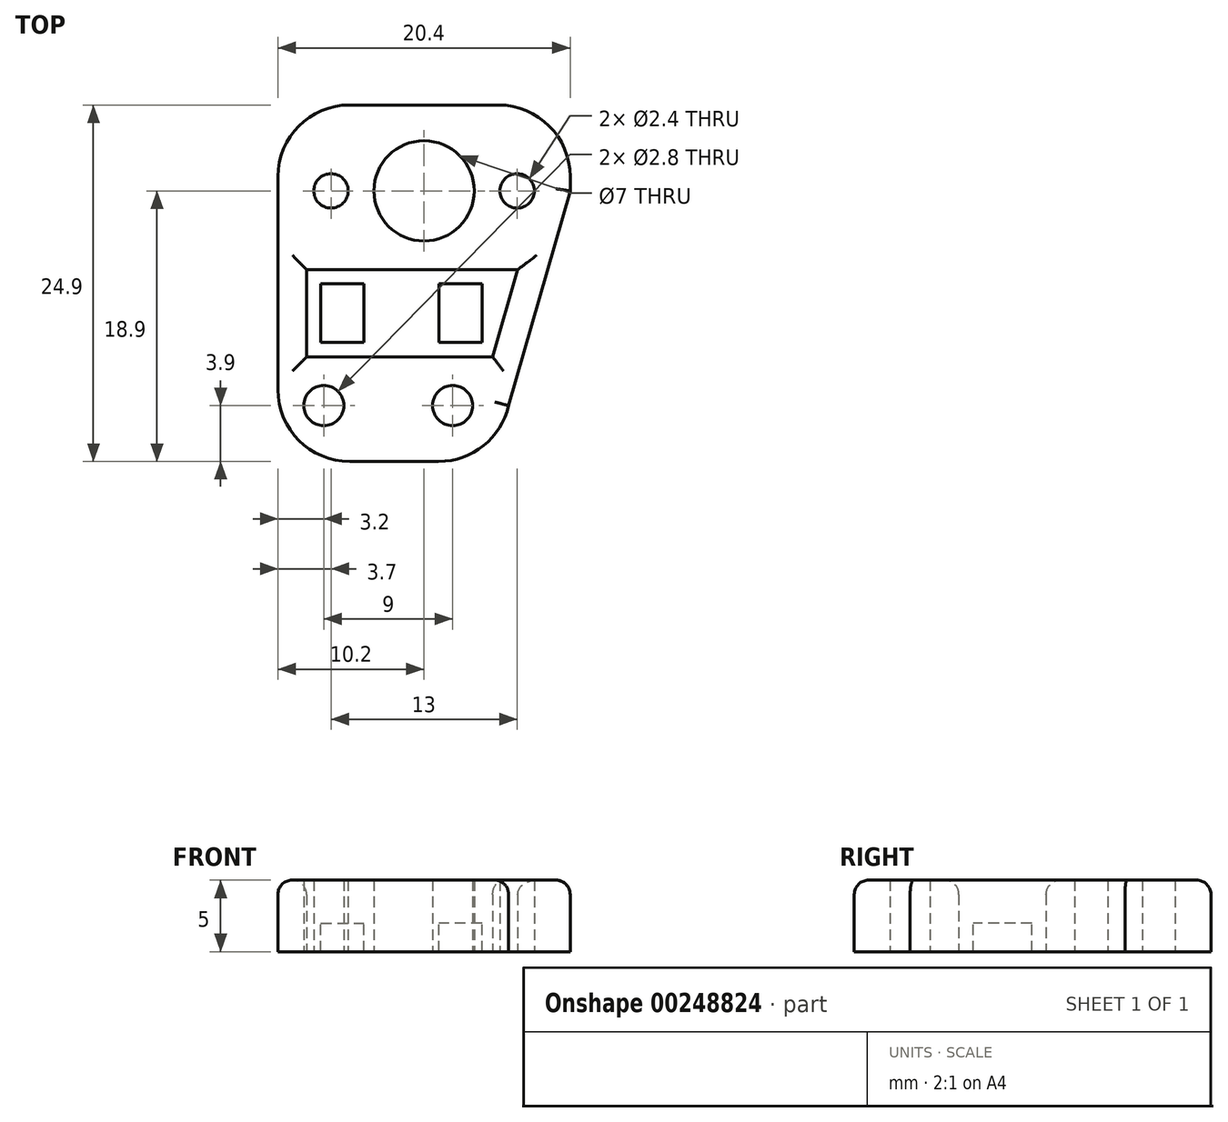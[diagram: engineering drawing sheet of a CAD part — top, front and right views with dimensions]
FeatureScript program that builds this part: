
annotation { "Feature Type Name" : "Feature", "Feature Type Description" : "" }
export const myFeature = defineFeature(function(context is Context, id is Id, definition is map)
    precondition{}
    {
        {
            var Q0;
            Q0=qCreatedBy(makeId("Top.planeOp"),FACE);
            var sketch = newSketch(context, id + "F0", { "sketchPlane" : qUnion([Q0])});
            skCircle(sketch, "E0", {"center": v(0, 0) * mm, "radius": 3.5 * mm});
            skCircle(sketch, "E1", {"center": v(-6.5, 0) * mm, "radius": 1.2 * mm});
            skCircle(sketch, "E2.MirrorC", {"center": v(6.5, 0) * mm, "radius": 1.2 * mm});
            skCircle(sketch, "E3", {"center": v(2, -15) * mm, "radius": 1.4 * mm});
            skCircle(sketch, "E4", {"center": v(-7, -15) * mm, "radius": 1.4 * mm});
            skLineSegment(sketch, "E5", {"start": v(-10.2, 6) * mm, "end": v(-10.2, -18.9) * mm});
            skLineSegment(sketch, "E6", {"start": v(-10.2, -18.9) * mm, "end": v(5.9, -18.9) * mm});
            skLineSegment(sketch, "E7", {"start": v(5.9, -18.9) * mm, "end": v(5.9, -15) * mm});
            skLineSegment(sketch, "E8", {"start": v(-10.2, 6) * mm, "end": v(10.2, 6) * mm});
            skLineSegment(sketch, "E9", {"start": v(10.2, 6) * mm, "end": v(10.2, 0) * mm});
            skLineSegment(sketch, "E10", {"start": v(10.2, 0) * mm, "end": v(5.9, -15) * mm});
            skLineSegment(sketch, "E11", {"start": v(-8.2, -11.6) * mm, "end": v(-8.2, -5.5) * mm});
            skLineSegment(sketch, "E12", {"start": v(-8.2, -5.5) * mm, "end": v(6.54, -5.5) * mm});
            skLineSegment(sketch, "E13", {"start": v(6.54, -5.5) * mm, "end": v(4.8, -11.6) * mm});
            skLineSegment(sketch, "E14", {"start": v(4.8, -11.6) * mm, "end": v(-8.2, -11.6) * mm});
            skSolve(sketch);
        }
        {
            var Q0;
            Q0=makeQuery(id+"F0.imprint","IMPRINT",FACE,{"disambiguationData":[TD([[makeQuery(id+"F0.imprint","IMPRINT",EDGE,{"derivedFrom":sQuery(id+"F0.wireOp",EDGE,"E0")}),-1.0]])]});
            extrude(context, id + "F1", {"entities" : qUnion([Q0]), "depth" : 5 * mm});
        }
        {
            var Q0;
            Q0=makeQuery(id+"F1.opExtrude","SWEPT_EDGE",EDGE,{"disambiguationData":[OSD([sQuery(id+"F0.wireOp",EDGE,"E6"),sQuery(id+"F0.wireOp",EDGE,"E7")])]});
            var Q1;
            Q1=makeQuery(id+"F1.opExtrude","SWEPT_EDGE",EDGE,{"disambiguationData":[OSD([sQuery(id+"F0.wireOp",EDGE,"E5"),sQuery(id+"F0.wireOp",EDGE,"E6")])]});
            var Q2;
            Q2=makeQuery(id+"F1.opExtrude","SWEPT_EDGE",EDGE,{"disambiguationData":[OSD([sQuery(id+"F0.wireOp",EDGE,"E8"),sQuery(id+"F0.wireOp",EDGE,"E9")])]});
            var Q3;
            Q3=makeQuery(id+"F1.opExtrude","SWEPT_EDGE",EDGE,{"disambiguationData":[OSD([sQuery(id+"F0.wireOp",EDGE,"E5"),sQuery(id+"F0.wireOp",EDGE,"E8")])]});
            fillet(context, id + "F2", {"entities" : qUnion([Q0, Q1, Q2, Q3]), "radius" : 5 * mm, "tangentPropagation" : true, "allowEdgeOverflow" : false});
        }
        {
            var Q0;
            Q0=makeQuery(id+"F0.imprint","IMPRINT",FACE,{"disambiguationData":[TD([[makeQuery(id+"F0.imprint","IMPRINT",EDGE,{"derivedFrom":sQuery(id+"F0.wireOp",EDGE,"E11")}),-1.0]])]});
            extrude(context, id + "F3", {"entities" : qUnion([Q0]), "operationType" : NewBodyOperationType.ADD, "depth" : 2 * mm});
        }
        {
            var Q0;
            Q0=makeQuery(id+"F1.opExtrude","CAP_EDGE",EDGE,{"disambiguationData":[OSD([sQuery(id+"F0.wireOp",EDGE,"E5")])],"isStart":false});
            var Q1;
            Q1=makeQuery(id+"F1.opExtrude","CAP_EDGE",EDGE,{"disambiguationData":[OSD([sQuery(id+"F0.wireOp",EDGE,"E12")])],"isStart":false});
            var Q2;
            Q2=makeQuery(id+"F1.opExtrude","CAP_EDGE",EDGE,{"disambiguationData":[OSD([sQuery(id+"F0.wireOp",EDGE,"E11")])],"isStart":false});
            var Q3;
            Q3=makeQuery(id+"F1.opExtrude","CAP_EDGE",EDGE,{"disambiguationData":[OSD([sQuery(id+"F0.wireOp",EDGE,"E14")])],"isStart":false});
            var Q4;
            Q4=makeQuery(id+"F1.opExtrude","CAP_EDGE",EDGE,{"disambiguationData":[OSD([sQuery(id+"F0.wireOp",EDGE,"E13")])],"isStart":false});
            var Q5;
            Q5=makeQuery(id+"F3.opExtrude","CAP_EDGE",EDGE,{"disambiguationData":[OSD([sQuery(id+"F0.wireOp",EDGE,"E12")])],"isStart":false});
            var Q6;
            Q6=makeQuery(id+"F3.opExtrude","CAP_EDGE",EDGE,{"disambiguationData":[OSD([sQuery(id+"F0.wireOp",EDGE,"E11")])],"isStart":false});
            var Q7;
            Q7=makeQuery(id+"F3.opExtrude","CAP_EDGE",EDGE,{"disambiguationData":[OSD([sQuery(id+"F0.wireOp",EDGE,"E14")])],"isStart":false});
            var Q8;
            Q8=makeQuery(id+"F3.opExtrude","CAP_EDGE",EDGE,{"disambiguationData":[OSD([sQuery(id+"F0.wireOp",EDGE,"E13")])],"isStart":false});
            fillet(context, id + "F4", {"entities" : qUnion([Q0, Q1, Q2, Q3, Q4, Q5, Q6, Q7, Q8]), "radius" : 1 * mm, "tangentPropagation" : true, "allowEdgeOverflow" : false});
        }
        {
            var Q0;
            Q0=makeQuery(id+"F3.opExtrude","CAP_FACE",FACE,{"disambiguationData":[OSD([sQuery(id+"F0.wireOp",EDGE,"E11"),sQuery(id+"F0.wireOp",EDGE,"E12"),sQuery(id+"F0.wireOp",EDGE,"E13"),sQuery(id+"F0.wireOp",EDGE,"E14")])],"isStart":false});
            var sketch = newSketch(context, id + "F5", { "sketchPlane" : qUnion([Q0])});
            skLineSegment(sketch, "E15.bottom", {"start": v(-7.2, -6.5) * mm, "end": v(-4.2, -6.5) * mm});
            skLineSegment(sketch, "E15.top", {"start": v(-7.2, -10.6) * mm, "end": v(-4.2, -10.6) * mm});
            skLineSegment(sketch, "E15.left", {"start": v(-7.2, -6.5) * mm, "end": v(-7.2, -10.6) * mm});
            skLineSegment(sketch, "E15.right", {"start": v(-4.2, -6.5) * mm, "end": v(-4.2, -10.6) * mm});
            skLineSegment(sketch, "E16.bottom", {"start": v(4.04, -10.6) * mm, "end": v(1.04, -10.6) * mm});
            skLineSegment(sketch, "E16.top", {"start": v(4.04, -6.5) * mm, "end": v(1.04, -6.5) * mm});
            skLineSegment(sketch, "E16.left", {"start": v(4.04, -10.6) * mm, "end": v(4.04, -6.5) * mm});
            skLineSegment(sketch, "E16.right", {"start": v(1.04, -10.6) * mm, "end": v(1.04, -6.5) * mm});
            skSolve(sketch);
        }
        {
            var Q0;
            Q0=makeQuery(id+"F5.imprint","IMPRINT",FACE,{"disambiguationData":[TD([[makeQuery(id+"F5.imprint","IMPRINT",EDGE,{"derivedFrom":sQuery(id+"F5.wireOp",EDGE,"E15.bottom")}),1.0]])]});
            var Q1;
            Q1=makeQuery(id+"F5.imprint","IMPRINT",FACE,{"disambiguationData":[TD([[makeQuery(id+"F5.imprint","IMPRINT",EDGE,{"derivedFrom":sQuery(id+"F5.wireOp",EDGE,"E16.bottom")}),1.0]])]});
            extrude(context, id + "F6", {"entities" : qUnion([Q0, Q1]), "operationType" : NewBodyOperationType.REMOVE, "oppositeDirection" : true, "depth" : 25 * mm});
        }
    });
